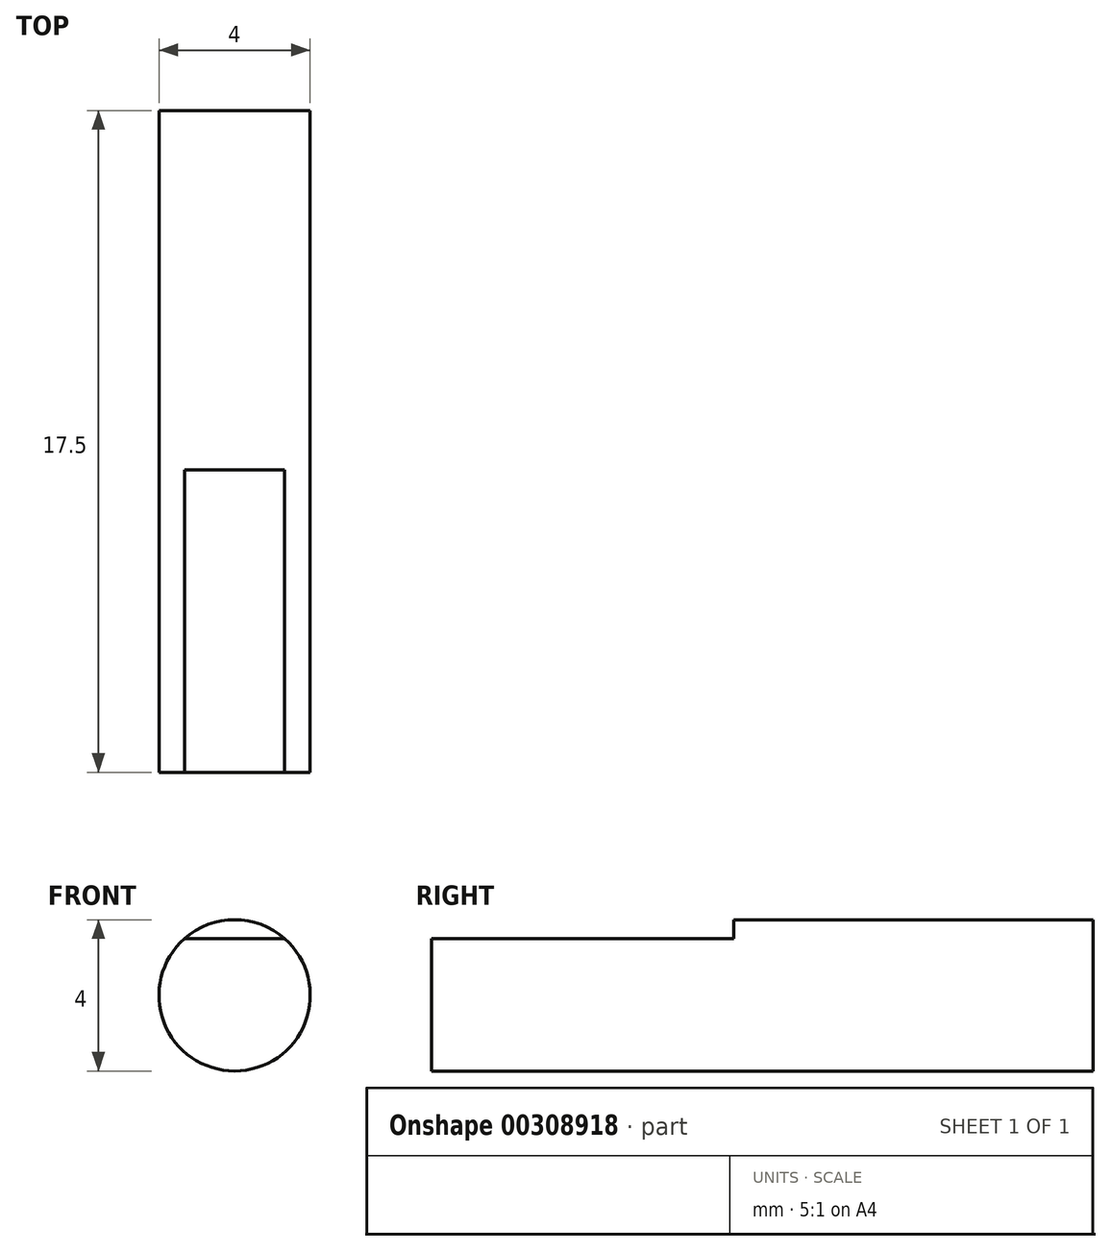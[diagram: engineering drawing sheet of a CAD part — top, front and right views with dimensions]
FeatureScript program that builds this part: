
annotation { "Feature Type Name" : "Feature", "Feature Type Description" : "" }
export const myFeature = defineFeature(function(context is Context, id is Id, definition is map)
    precondition{}
    {
        {
            var Q0;
            Q0=qCreatedBy(makeId("Front.planeOp"),FACE);
            var sketch = newSketch(context, id + "F0", { "sketchPlane" : qUnion([Q0])});
            skCircle(sketch, "E0", {"center": v(0, 0) * mm, "radius": 2 * mm});
            skSolve(sketch);
        }
        {
            var Q0;
            Q0 = qSketchRegion(id + "F0", true);
            extrude(context, id + "F1", {"entities" : qUnion([Q0]), "depth" : 17.5 * mm});
        }
        {
            var Q0;
            Q0=makeQuery(id+"F1.opExtrude","CAP_FACE",FACE,{"disambiguationData":[OSD([sQuery(id+"F0.wireOp",EDGE,"E0")])],"isStart":false});
            var sketch = newSketch(context, id + "F2", { "sketchPlane" : qUnion([Q0]), "disableImprinting" : false});
            skLineSegment(sketch, "E1", {"start": v(-1.32, 1.5) * mm, "end": v(1.32, 1.5) * mm});
            skArc(sketch, "E2", {"start": v(1.32, 1.5) * mm, "mid": v(0, 2) * mm, "end": v(-1.32, 1.5) * mm});
            skSolve(sketch);
        }
        {
            var Q0;
            Q0 = qSketchRegion(id + "F2", true);
            extrude(context, id + "F3", {"entities" : qUnion([Q0]), "operationType" : NewBodyOperationType.REMOVE, "oppositeDirection" : true, "depth" : 8 * mm});
        }
    });
